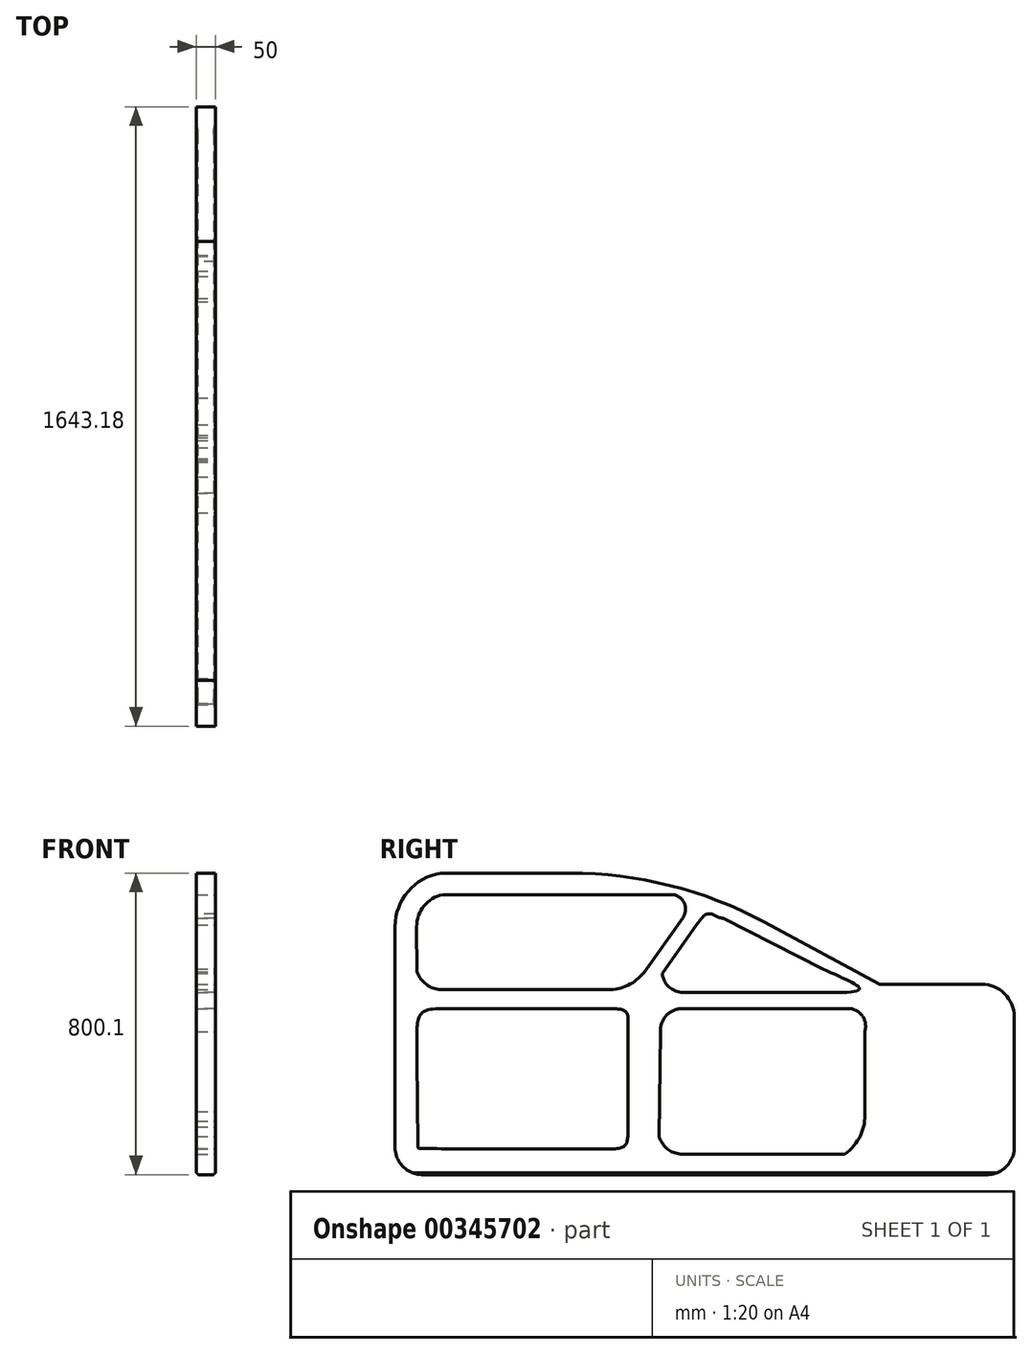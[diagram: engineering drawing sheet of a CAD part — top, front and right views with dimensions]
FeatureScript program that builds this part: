
annotation { "Feature Type Name" : "Feature", "Feature Type Description" : "" }
export const myFeature = defineFeature(function(context is Context, id is Id, definition is map)
    precondition{}
    {
        {
            var Q0;
            Q0=qCreatedBy(makeId("Right.planeOp"),FACE);
            var sketch = newSketch(context, id + "F0", { "sketchPlane" : qUnion([Q0])});
            skLineSegment(sketch, "E0", {"start": v(-818.74, 445.14) * mm, "end": v(-202.24, 445.14) * mm});
            skLineSegment(sketch, "E1", {"start": v(-202.24, 445.14) * mm, "end": v(345.98, 150.23) * mm});
            skLineSegment(sketch, "E2", {"start": v(345.98, 150.23) * mm, "end": v(1059.63, 150.23) * mm});
            skLineSegment(sketch, "E3", {"start": v(1059.63, 150.23) * mm, "end": v(1059.63, -354.96) * mm});
            skLineSegment(sketch, "E4", {"start": v(1059.63, -354.96) * mm, "end": v(-940.37, -354.96) * mm});
            skLineSegment(sketch, "E5", {"start": v(-940.37, -354.96) * mm, "end": v(-940.37, 302.69) * mm});
            skArc(sketch, "E6", {"start": v(-940.37, 302.69) * mm, "mid": v(-905.82, 396.34) * mm, "end": v(-818.74, 445.14) * mm});
            skLineSegment(sketch, "E7.0", {"start": v(-813.66, 387.99) * mm, "end": v(-202.24, 387.99) * mm});
            skArc(sketch, "E7.1", {"start": v(-883.22, 302.69) * mm, "mid": v(-863.62, 357.72) * mm, "end": v(-813.66, 387.99) * mm});
            skLineSegment(sketch, "E7.2", {"start": v(-882.25, 182.65) * mm, "end": v(-883.22, 302.69) * mm});
            skArc(sketch, "E8", {"start": v(-882.25, 182.65) * mm, "mid": v(-857.23, 149.4) * mm, "end": v(-818.03, 135.44) * mm});
            skLineSegment(sketch, "E9", {"start": v(-818.03, 135.44) * mm, "end": v(-375.15, 135.44) * mm});
            skLineSegment(sketch, "E10", {"start": v(-176.64, 326.96) * mm, "end": v(-279.6, 182.1) * mm});
            skArc(sketch, "E11", {"start": v(-375.15, 135.44) * mm, "mid": v(-321.98, 147.73) * mm, "end": v(-279.6, 182.1) * mm});
            skArc(sketch, "E12", {"start": v(-176.64, 326.96) * mm, "mid": v(-172.47, 364.6) * mm, "end": v(-202.24, 387.99) * mm});
            skLineSegment(sketch, "E13.0", {"start": v(-140.51, 307.02) * mm, "end": v(-231.15, 179.5) * mm});
            skLineSegment(sketch, "E14", {"start": v(-69.57, 325.78) * mm, "end": v(194.95, 191.14) * mm});
            skLineSegment(sketch, "E15", {"start": v(-175.6, 128.14) * mm, "end": v(185.83, 128.14) * mm});
            skArc(sketch, "E16", {"start": v(-231.15, 179.5) * mm, "mid": v(-213.43, 142.95) * mm, "end": v(-175.6, 128.14) * mm});
            skFitSpline(sketch, "E17", {"points": [v(-140.51, 307.02) * mm, v(-69.57, 325.78) * mm], "startDerivative": vector(101.12, 167.17) * mm, "endDerivative": vector(75.5, 5.18) * mm});
            skFitSpline(sketch, "E18", {"points": [v(194.95, 191.14) * mm, v(185.83, 128.14) * mm], "startDerivative": vector(247.53, -120.81) * mm, "endDerivative": vector(-546.75, 11.27) * mm});
            skLineSegment(sketch, "E19.0", {"start": v(-818.03, -286.56) * mm, "end": v(-375.15, -286.56) * mm});
            skLineSegment(sketch, "E20.0", {"start": v(-818.03, 85.44) * mm, "end": v(-375.15, 85.44) * mm});
            skLineSegment(sketch, "E21", {"start": v(-882.73, 0) * mm, "end": v(-881, -213.63) * mm});
            skPoint(sketch, "E21.startSnap0", {"position": v(-882.73, 242.67) * mm});
            skLineSegment(sketch, "E22", {"start": v(-321.98, 48.85) * mm, "end": v(-321.98, -227.83) * mm});
            skPoint(sketch, "E22.startSnap0", {"position": v(-321.98, 147.73) * mm});
            skFitSpline(sketch, "E23", {"points": [v(-882.73, 0) * mm, v(-818.03, 85.44) * mm], "startDerivative": vector(-1.36, 192) * mm, "endDerivative": vector(191.26, -2.6) * mm});
            skFitSpline(sketch, "E24", {"points": [v(-375.15, 85.44) * mm, v(-321.98, 48.85) * mm], "startDerivative": vector(150.7, 0.3) * mm, "endDerivative": vector(-0.85, -92.47) * mm});
            skFitSpline(sketch, "E25", {"points": [v(-881, -213.63) * mm, v(-818.03, -286.56) * mm], "startDerivative": vector(25.76, -289.53) * mm, "endDerivative": vector(261.62, -20.72) * mm});
            skFitSpline(sketch, "E26", {"points": [v(-375.15, -286.56) * mm, v(-321.98, -227.83) * mm], "startDerivative": vector(163.04, -5.64) * mm, "endDerivative": vector(2.4, 140.44) * mm});
            skArc(sketch, "E27", {"start": v(252.5, -300.3) * mm, "mid": v(294.54, -251.45) * mm, "end": v(306.07, -188.05) * mm});
            skArc(sketch, "E28", {"start": v(306.07, 24.44) * mm, "mid": v(300.83, 64.4) * mm, "end": v(266.45, 85.44) * mm});
            skArc(sketch, "E29", {"start": v(-239.7, -254.48) * mm, "mid": v(-218.4, -286.29) * mm, "end": v(-182.77, -300.3) * mm});
            skArc(sketch, "E30", {"start": v(-175.02, 85.44) * mm, "mid": v(-219.22, 68.57) * mm, "end": v(-236.27, 24.44) * mm});
            skLineSegment(sketch, "E31", {"start": v(266.45, 85.44) * mm, "end": v(-175.02, 85.44) * mm});
            skLineSegment(sketch, "E32", {"start": v(306.07, -188.05) * mm, "end": v(306.07, 24.44) * mm});
            skLineSegment(sketch, "E33", {"start": v(-239.7, -254.48) * mm, "end": v(-236.27, 24.44) * mm});
            skLineSegment(sketch, "E34", {"start": v(252.5, -300.3) * mm, "end": v(-182.77, -300.3) * mm});
            skLineSegment(sketch, "E35", {"start": v(345.98, 150.23) * mm, "end": v(345.98, -354.96) * mm});
            skLineSegment(sketch, "E36", {"start": v(702.8, 150.23) * mm, "end": v(702.8, -354.96) * mm});
            skSolve(sketch);
        }
        {
            var Q0;
            Q0=makeQuery(id+"F0.imprint","IMPRINT",FACE,{"disambiguationData":[TD([[makeQuery(id+"F0.imprint","IMPRINT",EDGE,{"derivedFrom":sQuery(id+"F0.wireOp",EDGE,"E0")}),-1.0]])]});
            var Q1;
            {var subQ0=sQuery(id+"F0.wireOp",EDGE,"E35");Q1=makeQuery(id+"F0.imprint","IMPRINT",FACE,{"disambiguationData":[TD([[makeQuery(id+"F0.imprint","IMPRINT",EDGE,{"derivedFrom":subQ0}),1.0]])]});}
            extrude(context, id + "F1", {"entities" : qUnion([Q0, Q1]), "oppositeDirection" : true, "depth" : 50 * mm});
        }
        {
            var Q0;
            Q0=makeQuery(id+"F1.opExtrude","SWEPT_EDGE",EDGE,{"disambiguationData":[OSD([sQuery(id+"F0.wireOp",EDGE,"E0"),sQuery(id+"F0.wireOp",EDGE,"E1")])]});
            fillet(context, id + "F2", {"entities" : qUnion([Q0]), "radius" : 1088.4 * mm, "tangentPropagation" : true, "allowEdgeOverflow" : false});
        }
        {
            var Q0;
            Q0=makeQuery(id+"F1.opExtrude","SWEPT_EDGE",EDGE,{"disambiguationData":[OSD([sQuery(id+"F0.wireOp",EDGE,"E2"),sQuery(id+"F0.wireOp",EDGE,"E3")])]});
            fillet(context, id + "F3", {"entities" : qUnion([Q0]), "radius" : 86.9 * mm, "tangentPropagation" : true, "allowEdgeOverflow" : false});
        }
        {
            var Q0;
            Q0=makeQuery(id+"F1.opExtrude","CAP_EDGE",EDGE,{"disambiguationData":[OSD([sQuery(id+"F0.wireOp",EDGE,"E4")])],"isStart":true});
            var Q1;
            Q1=makeQuery(id+"F1.opExtrude","CAP_EDGE",EDGE,{"disambiguationData":[OSD([sQuery(id+"F0.wireOp",EDGE,"E4")])],"isStart":false});
            chamfer(context, id + "F4", {"entities" : qUnion([Q0, Q1]), "width" : 5 * mm, "tangentPropagation" : true});
        }
        {
            var Q0;
            Q0=makeQuery(id+"F1.opExtrude","SWEPT_EDGE",EDGE,{"disambiguationData":[OSD([sQuery(id+"F0.wireOp",EDGE,"E3"),sQuery(id+"F0.wireOp",EDGE,"E4")])]});
            fillet(context, id + "F5", {"entities" : qUnion([Q0]), "radius" : 72.43 * mm, "tangentPropagation" : true, "allowEdgeOverflow" : false});
        }
    });
